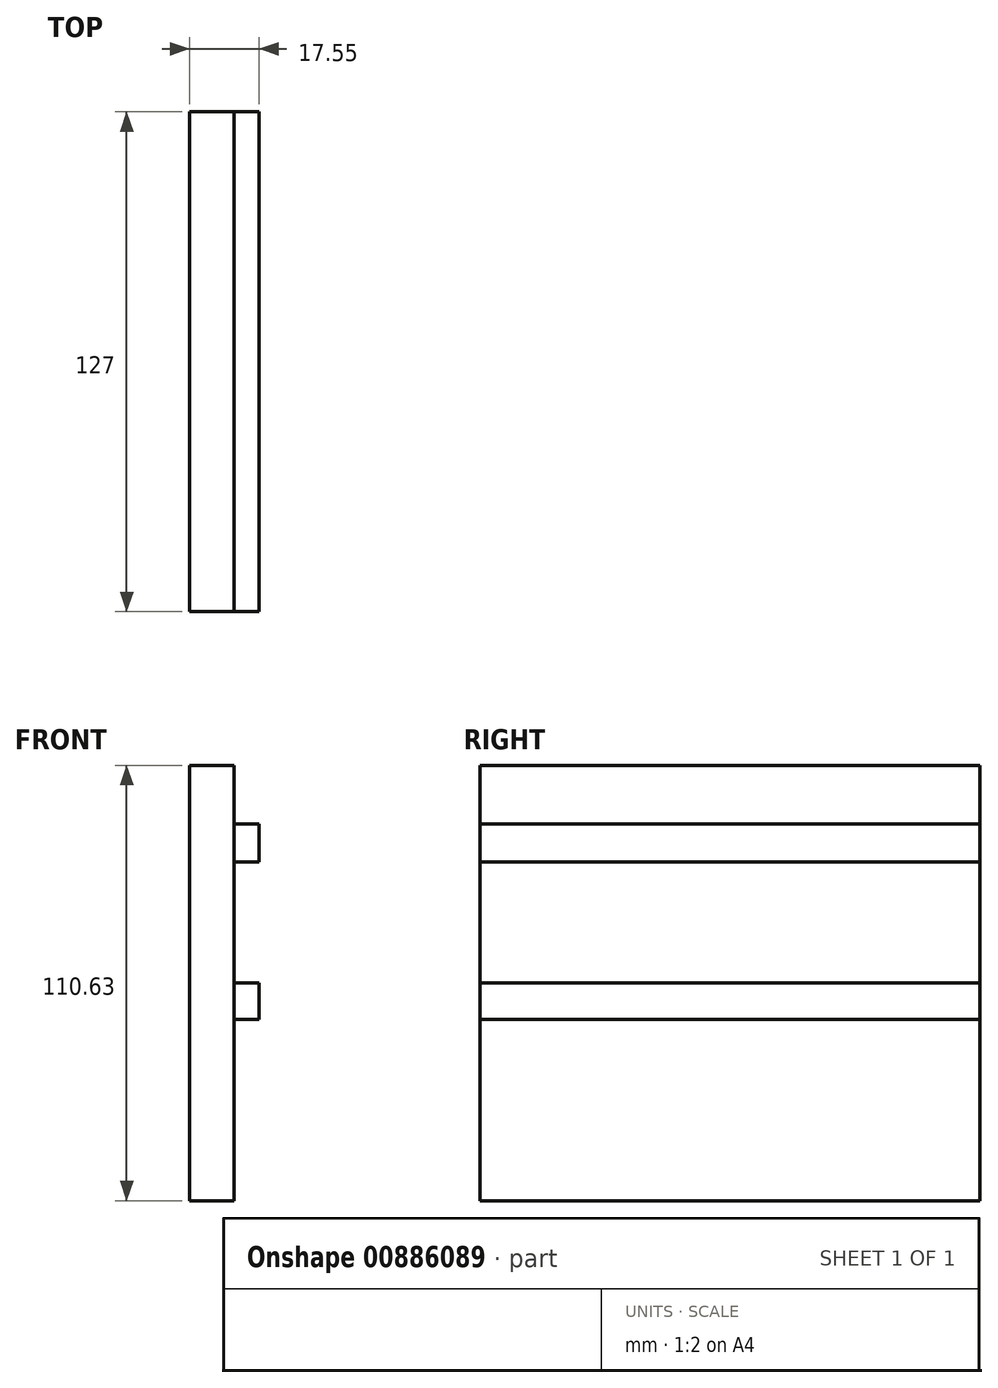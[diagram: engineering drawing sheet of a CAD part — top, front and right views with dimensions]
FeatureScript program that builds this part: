
annotation { "Feature Type Name" : "Feature", "Feature Type Description" : "" }
export const myFeature = defineFeature(function(context is Context, id is Id, definition is map)
    precondition{}
    {
        {
            var Q0;
            Q0=qCreatedBy(makeId("Front.planeOp"),FACE);
            var sketch = newSketch(context, id + "F0", { "sketchPlane" : qUnion([Q0])});
            skLineSegment(sketch, "E0.bottom", {"start": v(-56.47, 41.65) * mm, "end": v(-45.27, 41.65) * mm});
            skLineSegment(sketch, "E0.top", {"start": v(-56.47, -68.98) * mm, "end": v(-45.27, -68.98) * mm});
            skLineSegment(sketch, "E0.left", {"start": v(-56.47, 41.65) * mm, "end": v(-56.47, -68.98) * mm});
            skLineSegment(sketch, "E0.right", {"start": v(-45.27, 41.65) * mm, "end": v(-45.27, -68.98) * mm});
            skSolve(sketch);
        }
        {
            var Q0;
            Q0=makeQuery(id+"F0.imprint","IMPRINT",FACE,{"disambiguationData":[TD([[makeQuery(id+"F0.imprint","IMPRINT",EDGE,{"derivedFrom":sQuery(id+"F0.wireOp",EDGE,"E0.bottom")}),-1.0]])]});
            extrude(context, id + "F1", {"entities" : qUnion([Q0]), "oppositeDirection" : true, "depth" : 127 * mm, "offsetDistance" : 25.4 * mm});
        }
        {
            var Q0;
            Q0=makeQuery(id+"F1.opExtrude","SWEPT_FACE",FACE,{"disambiguationData":[OSD([sQuery(id+"F0.wireOp",EDGE,"E0.right")])]});
            var sketch = newSketch(context, id + "F2", { "sketchPlane" : qUnion([Q0])});
            skLineSegment(sketch, "E1.bottom", {"start": v(0, 26.7) * mm, "end": v(127, 26.7) * mm});
            skLineSegment(sketch, "E1.top", {"start": v(0, 17.03) * mm, "end": v(127, 17.03) * mm});
            skLineSegment(sketch, "E1.left", {"start": v(0, 26.7) * mm, "end": v(0, 17.03) * mm});
            skLineSegment(sketch, "E1.right", {"start": v(127, 26.7) * mm, "end": v(127, 17.03) * mm});
            skLineSegment(sketch, "E2.bottom", {"start": v(0, -13.66) * mm, "end": v(127, -13.66) * mm});
            skLineSegment(sketch, "E2.top", {"start": v(0, -22.9) * mm, "end": v(127, -22.9) * mm});
            skLineSegment(sketch, "E2.left", {"start": v(0, -13.66) * mm, "end": v(0, -22.9) * mm});
            skLineSegment(sketch, "E2.right", {"start": v(127, -13.66) * mm, "end": v(127, -22.9) * mm});
            skSolve(sketch);
        }
        {
            var Q0;
            Q0=makeQuery(id+"F2.imprint","IMPRINT",FACE,{"disambiguationData":[TD([[makeQuery(id+"F2.imprint","IMPRINT",EDGE,{"derivedFrom":sQuery(id+"F2.wireOp",EDGE,"E1.bottom")}),-1.0]])]});
            var Q1;
            Q1=makeQuery(id+"F2.imprint","IMPRINT",FACE,{"disambiguationData":[TD([[makeQuery(id+"F2.imprint","IMPRINT",EDGE,{"derivedFrom":sQuery(id+"F2.wireOp",EDGE,"E2.bottom")}),-1.0]])]});
            extrude(context, id + "F3", {"entities" : qUnion([Q0, Q1]), "depth" : 6.35 * mm, "offsetDistance" : 25.4 * mm});
        }
    });
